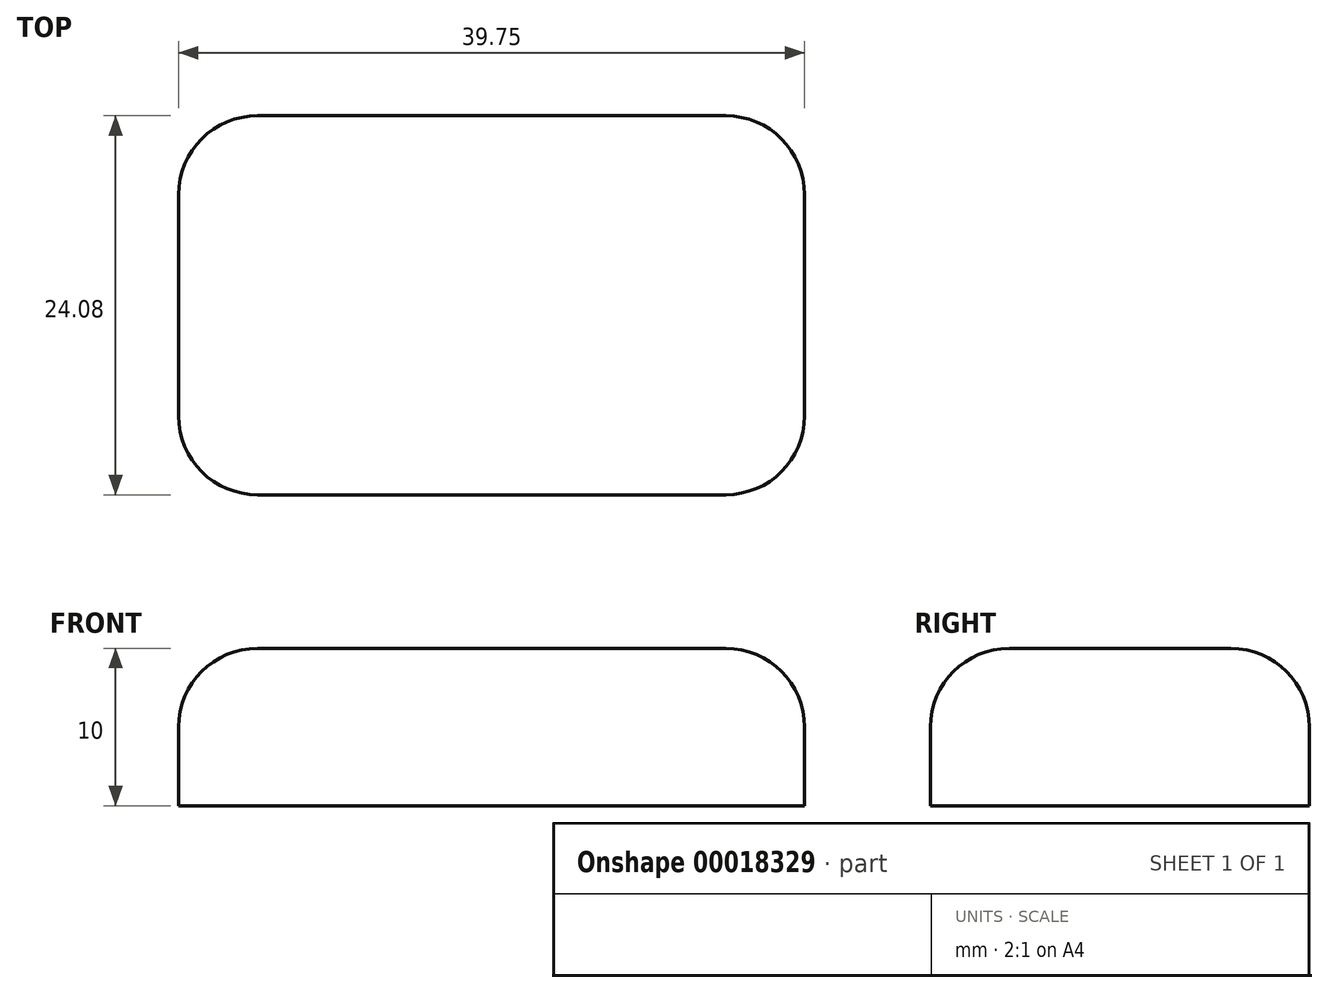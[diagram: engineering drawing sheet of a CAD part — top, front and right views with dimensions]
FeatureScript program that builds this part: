
annotation { "Feature Type Name" : "Feature", "Feature Type Description" : "" }
export const myFeature = defineFeature(function(context is Context, id is Id, definition is map)
    precondition{}
    {
        {
            var Q0;
            Q0=qCreatedBy(makeId("Top.planeOp"),FACE);
            var sketch = newSketch(context, id + "F0", { "sketchPlane" : qUnion([Q0])});
            skLineSegment(sketch, "E0.bottom", {"start": v(-17.73, 11.48) * mm, "end": v(22.02, 11.48) * mm});
            skLineSegment(sketch, "E0.top", {"start": v(-17.73, -12.6) * mm, "end": v(22.02, -12.6) * mm});
            skLineSegment(sketch, "E0.left", {"start": v(-17.73, 11.48) * mm, "end": v(-17.73, -12.6) * mm});
            skLineSegment(sketch, "E0.right", {"start": v(22.02, 11.48) * mm, "end": v(22.02, -12.6) * mm});
            skSolve(sketch);
        }
        {
            var Q0;
            Q0 = qSketchRegion(id + "F0", true);
            extrude(context, id + "F1", {"entities" : qUnion([Q0]), "depth" : 10 * mm, "offsetDistance" : 25 * mm});
        }
        {
            var Q0;
            Q0=makeQuery(id+"F1.opExtrude","CAP_EDGE",EDGE,{"disambiguationData":[OSD([sQuery(id+"F0.wireOp",EDGE,"E0.top")])],"isStart":false});
            fillet(context, id + "F2", {"entities" : qUnion([Q0]), "radius" : 5 * mm, "tangentPropagation" : true, "allowEdgeOverflow" : false});
        }
        {
            var Q0;
            Q0=makeQuery(id+"F1.opExtrude","CAP_EDGE",EDGE,{"disambiguationData":[OSD([sQuery(id+"F0.wireOp",EDGE,"E0.bottom")])],"isStart":false});
            var Q1;
            Q1=makeQuery(id+"F1.opExtrude","CAP_EDGE",EDGE,{"disambiguationData":[OSD([sQuery(id+"F0.wireOp",EDGE,"E0.right")])],"isStart":false});
            fillet(context, id + "F3", {"entities" : qUnion([Q0, Q1]), "radius" : 5 * mm, "tangentPropagation" : true, "allowEdgeOverflow" : false});
        }
        {
            var Q0;
            Q0=makeQuery(id+"F1.opExtrude","CAP_EDGE",EDGE,{"disambiguationData":[OSD([sQuery(id+"F0.wireOp",EDGE,"E0.left")])],"isStart":false});
            fillet(context, id + "F4", {"entities" : qUnion([Q0]), "radius" : 5 * mm, "tangentPropagation" : true, "allowEdgeOverflow" : false});
        }
        {
            var Q0;
            Q0=makeQuery(id+"F3.opFillet","BLEND_EDGE",EDGE,{"blendedFrom":[makeQuery(id+"F1.opExtrude","CAP_EDGE",EDGE,{"disambiguationData":[OSD([sQuery(id+"F0.wireOp",EDGE,"E0.bottom")])],"isStart":false}),makeQuery(id+"F1.opExtrude","CAP_EDGE",EDGE,{"disambiguationData":[OSD([sQuery(id+"F0.wireOp",EDGE,"E0.right")])],"isStart":false})],"blendedInto":[]});
            fillet(context, id + "F5", {"entities" : qUnion([Q0]), "radius" : 5 * mm, "tangentPropagation" : true, "allowEdgeOverflow" : false});
        }
    });
